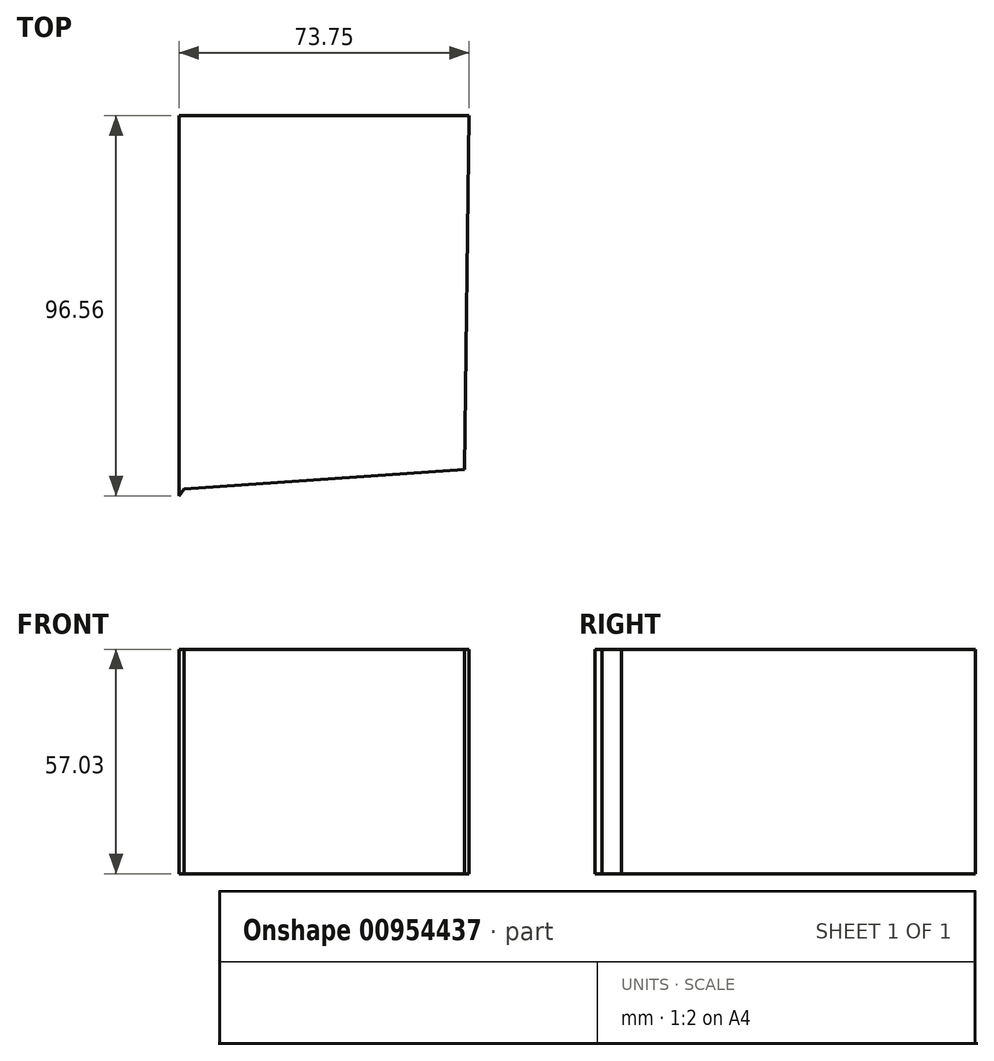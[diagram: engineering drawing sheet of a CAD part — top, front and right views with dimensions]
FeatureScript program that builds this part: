
annotation { "Feature Type Name" : "Feature", "Feature Type Description" : "" }
export const myFeature = defineFeature(function(context is Context, id is Id, definition is map)
    precondition{}
    {
        {
            var Q0;
            Q0=qCreatedBy(makeId("Top.planeOp"),FACE);
            var sketch = newSketch(context, id + "F0", { "sketchPlane" : qUnion([Q0])});
            skLineSegment(sketch, "E0", {"start": v(-39.6, -42.96) * mm, "end": v(-39.6, 53.6) * mm});
            skLineSegment(sketch, "E1", {"start": v(-39.6, 53.6) * mm, "end": v(34.15, 53.6) * mm});
            skLineSegment(sketch, "E2", {"start": v(34.15, 53.6) * mm, "end": v(33.01, -36.25) * mm});
            skLineSegment(sketch, "E3", {"start": v(33.01, -36.25) * mm, "end": v(-38.33, -41.2) * mm});
            skLineSegment(sketch, "E4", {"start": v(-38.33, -41.2) * mm, "end": v(-39.6, -42.96) * mm});
            skSolve(sketch);
        }
        {
            var Q0;
            Q0=makeQuery(id+"F0.imprint","IMPRINT",FACE,{"disambiguationData":[TD([[makeQuery(id+"F0.imprint","IMPRINT",EDGE,{"derivedFrom":sQuery(id+"F0.wireOp",EDGE,"E0")}),-1.0]])]});
            var sketch = newSketch(context, id + "F1", { "sketchPlane" : qUnion([Q0])});
            skSolve(sketch);
        }
        {
            var Q0;
            Q0=makeQuery(id+"F1.imprint","IMPRINT",FACE,{"disambiguationData":[TD([[makeQuery(id+"F1.imprint","IMPRINT",EDGE,{"derivedFrom":makeQuery(id+"F0.imprint","IMPRINT",EDGE,{"derivedFrom":sQuery(id+"F0.wireOp",EDGE,"E0")})}),-1.0]])]});
            extrude(context, id + "F2", {"entities" : qUnion([Q0]), "depth" : 57.03 * mm, "offsetDistance" : 25 * mm});
        }
    });
